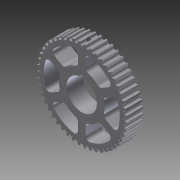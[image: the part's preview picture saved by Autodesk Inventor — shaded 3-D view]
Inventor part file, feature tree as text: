
AUTODESK INVENTOR PART (.ipt)
format: ipt  version: 2012 (Build 160160000, 160)  size: 630,272 bytes
history: native  units: in
note: dims shown in document units (in); Inventor stores cm internally (conversion verified against a paired STEP export)
features: extrude x4, sketch x3, fillet x1, plane x1, thread x1, imported_body x1
ambient origin geometry x8: Origin, YZ Plane, XZ Plane, XY Plane, X Axis, Y Axis, Z Axis, Center Point
feature tree (11):
  sketch  "Sketch1"  dims[d0=1.0in d1=1.0in d2=0.0in]
  extrude  "Extrusion1"  Depth=1.0in TaperAngle=0.0deg
  extrude  "Extrusion2"  Depth=0.125in
  extrude  "Extrusion3"  Depth=0.0625in
  fillet  "Fillet1"  Radius=0.4375in
  plane  "Work Plane1"
  extrude  "Extrusion4"  Depth=1.25in
  thread  "Thread1"  [1 undecoded]
  imported_body  "Base1"
  sketch  "Sketch2"  dims[d3=0.3925in d4=0.0in d5=0.125in]
  sketch  "Sketch3"  dims[d6=0.125in d7=0.0625in d8=0.4375in d9=1.25in d10=0.75in d11=60.0deg d12=0.125in d13=0.125in d14=2.3622in d16=360.0deg d18=1.0in d19=0.0in d20=0.125in d21=0.5445in d22=0.2722in d23=0.138in d24=2.0in d25=0.0in d26=1.0in d27=0.0in]
note: 1 required parameter value undecoded (feature->parameter linkage not recoverable at this tier; creation-order binding heuristic only, values carry confidence <= 0.55)
